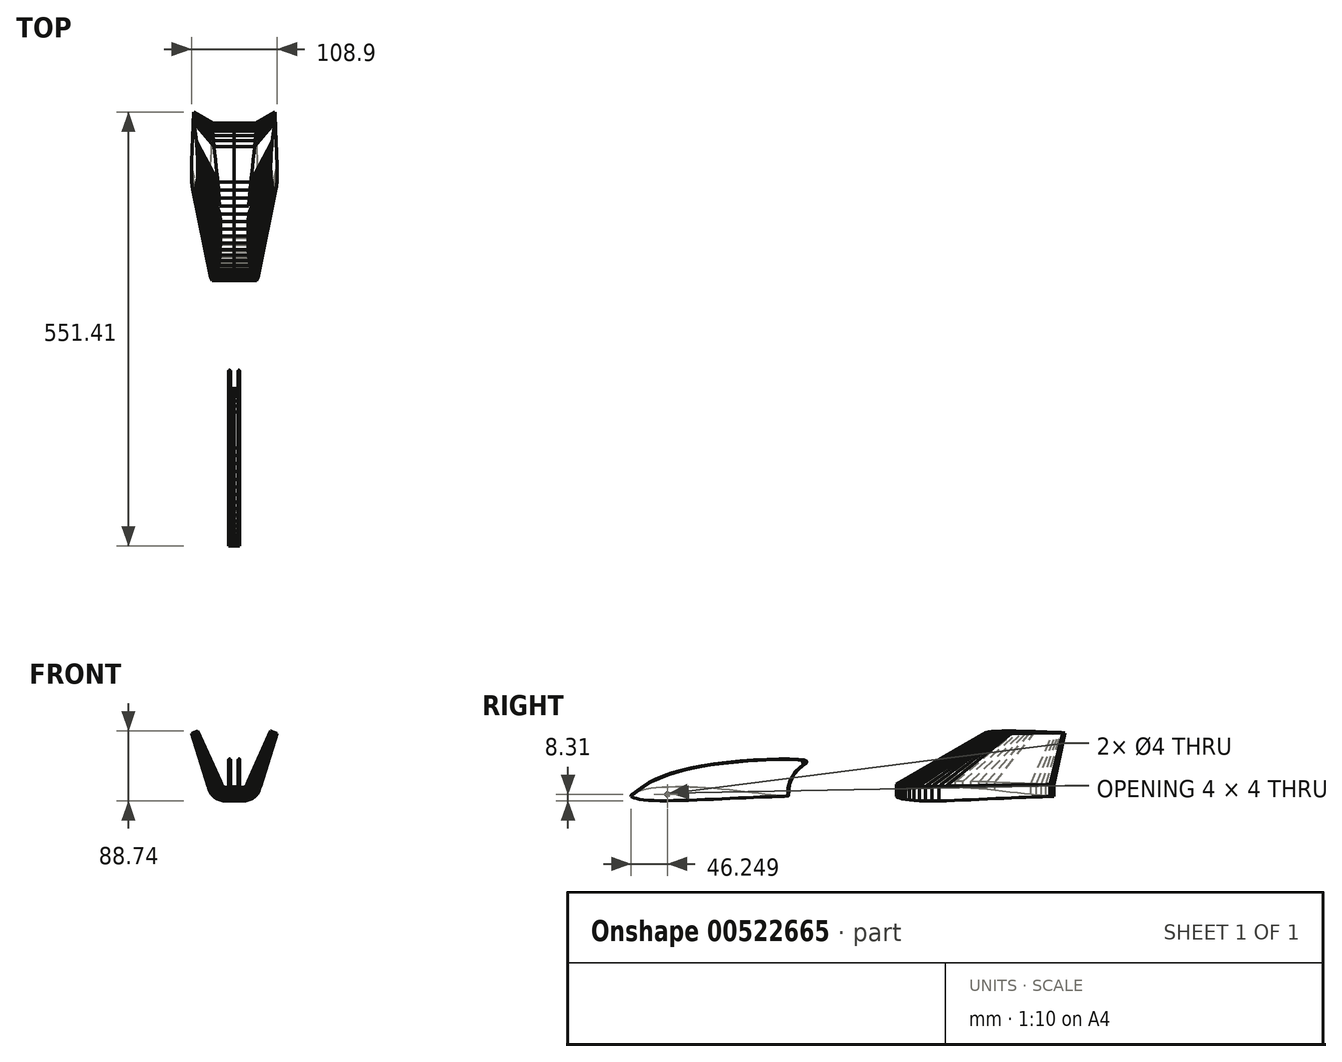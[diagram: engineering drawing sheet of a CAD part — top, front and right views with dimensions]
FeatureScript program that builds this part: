
annotation { "Feature Type Name" : "Feature", "Feature Type Description" : "" }
export const myFeature = defineFeature(function(context is Context, id is Id, definition is map)
    precondition{}
    {
        {
            var Q0;
            Q0=qCreatedBy(makeId("Right.planeOp"),FACE);
            var sketch = newSketch(context, id + "F0", { "sketchPlane" : qUnion([Q0])});
            skLineSegment(sketch, "E0.MirrorCS", {"start": v(124.06, -2.37) * mm, "end": v(124.69, -2.32) * mm});
            skLineSegment(sketch, "E1.MirrorCS", {"start": v(119.29, -2.62) * mm, "end": v(122.24, -2.48) * mm});
            skLineSegment(sketch, "E2.MirrorCS", {"start": v(122.24, -2.48) * mm, "end": v(124.06, -2.37) * mm});
            skLineSegment(sketch, "E3.MirrorCS", {"start": v(124.69, -2.32) * mm, "end": v(124.05, -2.33) * mm});
            skLineSegment(sketch, "E4.MirrorCS", {"start": v(124.05, -2.33) * mm, "end": v(122.1, -2.3) * mm});
            skLineSegment(sketch, "E5.MirrorCS", {"start": v(122.1, -2.3) * mm, "end": v(118.9, -2.2) * mm});
            skLineSegment(sketch, "E6.MirrorCS", {"start": v(-75.31, -2.32) * mm, "end": v(-75.15, -2.84) * mm});
            skLineSegment(sketch, "E7.MirrorCS", {"start": v(-61.33, 5) * mm, "end": v(-65.79, 3.73) * mm});
            skLineSegment(sketch, "E8.MirrorCS", {"start": v(115.22, -2.78) * mm, "end": v(119.29, -2.62) * mm});
            skLineSegment(sketch, "E9.MirrorCS", {"start": v(-65.79, 3.73) * mm, "end": v(-69.42, 2.35) * mm});
            skLineSegment(sketch, "E10.MirrorCS", {"start": v(-69.42, 2.35) * mm, "end": v(-72.2, 0.9) * mm});
            skLineSegment(sketch, "E11.MirrorCS", {"start": v(-72.2, 0.9) * mm, "end": v(-74.13, -0.52) * mm});
            skLineSegment(sketch, "E12.MirrorCS", {"start": v(-74.13, -0.52) * mm, "end": v(-75.2, -1.8) * mm});
            skLineSegment(sketch, "E13.MirrorCS", {"start": v(-75.2, -1.8) * mm, "end": v(-75.31, -2.32) * mm});
            skLineSegment(sketch, "E14.MirrorCS", {"start": v(-75.15, -2.84) * mm, "end": v(-73.93, -3.77) * mm});
            skLineSegment(sketch, "E15.MirrorCS", {"start": v(-73.93, -3.77) * mm, "end": v(-71.65, -4.72) * mm});
            skLineSegment(sketch, "E16.MirrorCS", {"start": v(118.9, -2.2) * mm, "end": v(114.52, -1.97) * mm});
            skLineSegment(sketch, "E17.MirrorCS", {"start": v(-68.38, -5.63) * mm, "end": v(-64.18, -6.45) * mm});
            skLineSegment(sketch, "E18.MirrorCS", {"start": v(-71.65, -4.72) * mm, "end": v(-68.38, -5.63) * mm});
            skLineSegment(sketch, "E19.MirrorCS", {"start": v(114.52, -1.97) * mm, "end": v(109.03, -1.58) * mm});
            skLineSegment(sketch, "E20.MirrorCS", {"start": v(109.03, -1.58) * mm, "end": v(102.52, -1) * mm});
            skLineSegment(sketch, "E21.MirrorCS", {"start": v(103.9, -3.2) * mm, "end": v(110.07, -2.97) * mm});
            skLineSegment(sketch, "E22.MirrorCS", {"start": v(110.07, -2.97) * mm, "end": v(115.22, -2.78) * mm});
            skLineSegment(sketch, "E23.MirrorCS", {"start": v(87, 0.67) * mm, "end": v(78.26, 1.71) * mm});
            skLineSegment(sketch, "E24.MirrorCS", {"start": v(-56.06, 6.14) * mm, "end": v(-61.33, 5) * mm});
            skLineSegment(sketch, "E25.MirrorCS", {"start": v(78.26, 1.71) * mm, "end": v(69.02, 2.84) * mm});
            skLineSegment(sketch, "E26.MirrorCS", {"start": v(-30.42, -8.31) * mm, "end": v(-21.47, -8.22) * mm});
            skLineSegment(sketch, "E27.MirrorCS", {"start": v(69.02, 2.84) * mm, "end": v(59.42, 3.99) * mm});
            skLineSegment(sketch, "E28.MirrorCS", {"start": v(-21.47, -8.22) * mm, "end": v(-11.95, -8) * mm});
            skLineSegment(sketch, "E29.MirrorCS", {"start": v(59.42, 3.99) * mm, "end": v(49.56, 5.1) * mm});
            skLineSegment(sketch, "E30.MirrorCS", {"start": v(-11.95, -8) * mm, "end": v(-1.98, -7.68) * mm});
            skLineSegment(sketch, "E31.MirrorCS", {"start": v(49.56, 5.1) * mm, "end": v(39.54, 6.12) * mm});
            skLineSegment(sketch, "E32.MirrorCS", {"start": v(-1.98, -7.68) * mm, "end": v(8.35, -7.28) * mm});
            skLineSegment(sketch, "E33.MirrorCS", {"start": v(8.35, -7.28) * mm, "end": v(18.91, -6.83) * mm});
            skLineSegment(sketch, "E34.MirrorCS", {"start": v(39.54, 6.12) * mm, "end": v(29.44, 7.02) * mm});
            skLineSegment(sketch, "E35.MirrorCS", {"start": v(18.91, -6.83) * mm, "end": v(29.6, -6.36) * mm});
            skLineSegment(sketch, "E36.MirrorCS", {"start": v(29.44, 7.02) * mm, "end": v(19.35, 7.76) * mm});
            skLineSegment(sketch, "E37.MirrorCS", {"start": v(29.6, -6.36) * mm, "end": v(40.26, -5.87) * mm});
            skLineSegment(sketch, "E38.MirrorCS", {"start": v(19.35, 7.76) * mm, "end": v(9.36, 8.35) * mm});
            skLineSegment(sketch, "E39.MirrorCS", {"start": v(40.26, -5.87) * mm, "end": v(50.78, -5.4) * mm});
            skLineSegment(sketch, "E40.MirrorCS", {"start": v(9.36, 8.35) * mm, "end": v(-0.44, 8.76) * mm});
            skLineSegment(sketch, "E41.MirrorCS", {"start": v(50.78, -5.4) * mm, "end": v(61.02, -4.95) * mm});
            skLineSegment(sketch, "E42.MirrorCS", {"start": v(-0.44, 8.76) * mm, "end": v(-9.94, 8.99) * mm});
            skLineSegment(sketch, "E43.MirrorCS", {"start": v(-19.05, 9.02) * mm, "end": v(-27.68, 8.86) * mm});
            skLineSegment(sketch, "E44.MirrorCS", {"start": v(70.86, -4.52) * mm, "end": v(80.18, -4.13) * mm});
            skLineSegment(sketch, "E45.MirrorCS", {"start": v(61.02, -4.95) * mm, "end": v(70.86, -4.52) * mm});
            skLineSegment(sketch, "E46.MirrorCS", {"start": v(-9.94, 8.99) * mm, "end": v(-19.05, 9.02) * mm});
            skLineSegment(sketch, "E47.MirrorCS", {"start": v(-27.68, 8.86) * mm, "end": v(-35.76, 8.48) * mm});
            skLineSegment(sketch, "E48.MirrorCS", {"start": v(80.18, -4.13) * mm, "end": v(88.87, -3.77) * mm});
            skLineSegment(sketch, "E49.MirrorCS", {"start": v(-64.18, -6.45) * mm, "end": v(-59.07, -7.15) * mm});
            skLineSegment(sketch, "E50.MirrorCS", {"start": v(-35.76, 8.48) * mm, "end": v(-43.22, 7.9) * mm});
            skLineSegment(sketch, "E51.MirrorCS", {"start": v(88.87, -3.77) * mm, "end": v(96.8, -3.46) * mm});
            skLineSegment(sketch, "E52.MirrorCS", {"start": v(-59.07, -7.15) * mm, "end": v(-53.1, -7.7) * mm});
            skLineSegment(sketch, "E53.MirrorCS", {"start": v(102.52, -1) * mm, "end": v(95.14, -0.25) * mm});
            skLineSegment(sketch, "E54.MirrorCS", {"start": v(-43.22, 7.9) * mm, "end": v(-50, 7.11) * mm});
            skLineSegment(sketch, "E55.MirrorCS", {"start": v(-53.1, -7.7) * mm, "end": v(-46.3, -8.07) * mm});
            skLineSegment(sketch, "E56.MirrorCS", {"start": v(96.8, -3.46) * mm, "end": v(103.9, -3.2) * mm});
            skLineSegment(sketch, "E57.MirrorCS", {"start": v(-50, 7.11) * mm, "end": v(-56.06, 6.14) * mm});
            skLineSegment(sketch, "E58.MirrorCS", {"start": v(95.14, -0.25) * mm, "end": v(87, 0.67) * mm});
            skLineSegment(sketch, "E59.MirrorCS", {"start": v(-46.3, -8.07) * mm, "end": v(-38.72, -8.27) * mm});
            skLineSegment(sketch, "E60.MirrorCS", {"start": v(-38.72, -8.27) * mm, "end": v(-30.42, -8.31) * mm});
            skLineSegment(sketch, "E61.MirrorCS", {"start": v(-213.27, -2.07) * mm, "end": v(-212.64, -2.02) * mm});
            skLineSegment(sketch, "E62.MirrorCS", {"start": v(-218.04, -2.32) * mm, "end": v(-215.09, -2.18) * mm});
            skLineSegment(sketch, "E63.MirrorCS", {"start": v(-215.09, -2.18) * mm, "end": v(-213.27, -2.07) * mm});
            skLineSegment(sketch, "E64.MirrorCS", {"start": v(-212.64, -2.02) * mm, "end": v(-213.29, -2.03) * mm});
            skLineSegment(sketch, "E65.MirrorCS", {"start": v(-213.29, -2.03) * mm, "end": v(-215.22, -2) * mm});
            skLineSegment(sketch, "E66.MirrorCS", {"start": v(-215.22, -2) * mm, "end": v(-218.42, -1.9) * mm});
            skLineSegment(sketch, "E67.MirrorCS", {"start": v(-412.64, -2.02) * mm, "end": v(-412.49, -2.54) * mm});
            skLineSegment(sketch, "E68.MirrorCS", {"start": v(-398.66, 5.3) * mm, "end": v(-403.12, 4.03) * mm});
            skLineSegment(sketch, "E69.MirrorCS", {"start": v(-222.12, -2.48) * mm, "end": v(-218.04, -2.32) * mm});
            skLineSegment(sketch, "E70.MirrorCS", {"start": v(-403.12, 4.03) * mm, "end": v(-406.75, 2.65) * mm});
            skLineSegment(sketch, "E71.MirrorCS", {"start": v(-406.75, 2.65) * mm, "end": v(-409.53, 1.2) * mm});
            skLineSegment(sketch, "E72.MirrorCS", {"start": v(-409.53, 1.2) * mm, "end": v(-411.46, -0.22) * mm});
            skLineSegment(sketch, "E73.MirrorCS", {"start": v(-411.46, -0.22) * mm, "end": v(-412.52, -1.5) * mm});
            skLineSegment(sketch, "E74.MirrorCS", {"start": v(-412.52, -1.5) * mm, "end": v(-412.64, -2.02) * mm});
            skLineSegment(sketch, "E75.MirrorCS", {"start": v(-412.49, -2.54) * mm, "end": v(-411.26, -3.47) * mm});
            skLineSegment(sketch, "E76.MirrorCS", {"start": v(-411.26, -3.47) * mm, "end": v(-408.98, -4.42) * mm});
            skLineSegment(sketch, "E77.MirrorCS", {"start": v(-218.42, -1.9) * mm, "end": v(-222.8, -1.67) * mm});
            skLineSegment(sketch, "E78.MirrorCS", {"start": v(-405.72, -5.33) * mm, "end": v(-401.5, -6.15) * mm});
            skLineSegment(sketch, "E79.MirrorCS", {"start": v(-408.98, -4.42) * mm, "end": v(-405.72, -5.33) * mm});
            skLineSegment(sketch, "E80.MirrorCS", {"start": v(-222.8, -1.67) * mm, "end": v(-228.3, -1.28) * mm});
            skLineSegment(sketch, "E81.MirrorCS", {"start": v(-228.3, -1.28) * mm, "end": v(-234.81, -0.7) * mm});
            skLineSegment(sketch, "E82.MirrorCS", {"start": v(-233.43, -2.9) * mm, "end": v(-227.27, -2.67) * mm});
            skLineSegment(sketch, "E83.MirrorCS", {"start": v(-227.27, -2.67) * mm, "end": v(-222.12, -2.48) * mm});
            skLineSegment(sketch, "E84.MirrorCS", {"start": v(-250.32, 0.97) * mm, "end": v(-259.07, 2.01) * mm});
            skLineSegment(sketch, "E85.MirrorCS", {"start": v(-393.39, 6.44) * mm, "end": v(-398.66, 5.3) * mm});
            skLineSegment(sketch, "E86.MirrorCS", {"start": v(-259.07, 2.01) * mm, "end": v(-268.3, 3.14) * mm});
            skLineSegment(sketch, "E87.MirrorCS", {"start": v(-367.75, -8.01) * mm, "end": v(-358.8, -7.92) * mm});
            skLineSegment(sketch, "E88.MirrorCS", {"start": v(-268.3, 3.14) * mm, "end": v(-277.91, 4.29) * mm});
            skLineSegment(sketch, "E89.MirrorCS", {"start": v(-358.8, -7.92) * mm, "end": v(-349.29, -7.7) * mm});
            skLineSegment(sketch, "E90.MirrorCS", {"start": v(-277.91, 4.29) * mm, "end": v(-287.77, 5.4) * mm});
            skLineSegment(sketch, "E91.MirrorCS", {"start": v(-349.29, -7.7) * mm, "end": v(-339.31, -7.38) * mm});
            skLineSegment(sketch, "E92.MirrorCS", {"start": v(-287.77, 5.4) * mm, "end": v(-297.79, 6.42) * mm});
            skLineSegment(sketch, "E93.MirrorCS", {"start": v(-339.31, -7.38) * mm, "end": v(-328.98, -6.98) * mm});
            skLineSegment(sketch, "E94.MirrorCS", {"start": v(-328.98, -6.98) * mm, "end": v(-318.42, -6.53) * mm});
            skLineSegment(sketch, "E95.MirrorCS", {"start": v(-297.79, 6.42) * mm, "end": v(-307.89, 7.32) * mm});
            skLineSegment(sketch, "E96.MirrorCS", {"start": v(-318.42, -6.53) * mm, "end": v(-307.74, -6.06) * mm});
            skLineSegment(sketch, "E97.MirrorCS", {"start": v(-307.89, 7.32) * mm, "end": v(-317.98, 8.06) * mm});
            skLineSegment(sketch, "E98.MirrorCS", {"start": v(-307.74, -6.06) * mm, "end": v(-297.07, -5.57) * mm});
            skLineSegment(sketch, "E99.MirrorCS", {"start": v(-317.98, 8.06) * mm, "end": v(-327.97, 8.65) * mm});
            skLineSegment(sketch, "E100.MirrorCS", {"start": v(-297.07, -5.57) * mm, "end": v(-286.55, -5.1) * mm});
            skLineSegment(sketch, "E101.MirrorCS", {"start": v(-327.97, 8.65) * mm, "end": v(-337.77, 9.06) * mm});
            skLineSegment(sketch, "E102.MirrorCS", {"start": v(-286.55, -5.1) * mm, "end": v(-276.3, -4.65) * mm});
            skLineSegment(sketch, "E103.MirrorCS", {"start": v(-337.77, 9.06) * mm, "end": v(-347.27, 9.29) * mm});
            skLineSegment(sketch, "E104.MirrorCS", {"start": v(-356.38, 9.32) * mm, "end": v(-365.01, 9.16) * mm});
            skLineSegment(sketch, "E105.MirrorCS", {"start": v(-266.47, -4.22) * mm, "end": v(-257.15, -3.83) * mm});
            skLineSegment(sketch, "E106.MirrorCS", {"start": v(-276.3, -4.65) * mm, "end": v(-266.47, -4.22) * mm});
            skLineSegment(sketch, "E107.MirrorCS", {"start": v(-347.27, 9.29) * mm, "end": v(-356.38, 9.32) * mm});
            skLineSegment(sketch, "E108.MirrorCS", {"start": v(-365.01, 9.16) * mm, "end": v(-373.1, 8.78) * mm});
            skLineSegment(sketch, "E109.MirrorCS", {"start": v(-257.15, -3.83) * mm, "end": v(-248.46, -3.47) * mm});
            skLineSegment(sketch, "E110.MirrorCS", {"start": v(-401.5, -6.15) * mm, "end": v(-396.4, -6.85) * mm});
            skLineSegment(sketch, "E111.MirrorCS", {"start": v(-373.1, 8.78) * mm, "end": v(-380.56, 8.2) * mm});
            skLineSegment(sketch, "E112.MirrorCS", {"start": v(-248.46, -3.47) * mm, "end": v(-240.52, -3.16) * mm});
            skLineSegment(sketch, "E113.MirrorCS", {"start": v(-396.4, -6.85) * mm, "end": v(-390.43, -7.4) * mm});
            skLineSegment(sketch, "E114.MirrorCS", {"start": v(-234.81, -0.7) * mm, "end": v(-242.2, 0.05) * mm});
            skLineSegment(sketch, "E115.MirrorCS", {"start": v(-380.56, 8.2) * mm, "end": v(-387.34, 7.41) * mm});
            skLineSegment(sketch, "E116.MirrorCS", {"start": v(-390.43, -7.4) * mm, "end": v(-383.63, -7.77) * mm});
            skLineSegment(sketch, "E117.MirrorCS", {"start": v(-240.52, -3.16) * mm, "end": v(-233.43, -2.9) * mm});
            skLineSegment(sketch, "E118.MirrorCS", {"start": v(-387.34, 7.41) * mm, "end": v(-393.39, 6.44) * mm});
            skLineSegment(sketch, "E119.MirrorCS", {"start": v(-242.2, 0.05) * mm, "end": v(-250.32, 0.97) * mm});
            skLineSegment(sketch, "E120.MirrorCS", {"start": v(-383.63, -7.77) * mm, "end": v(-376.06, -7.97) * mm});
            skLineSegment(sketch, "E121.MirrorCS", {"start": v(-376.06, -7.97) * mm, "end": v(-367.75, -8.01) * mm});
            skSolve(sketch);
        }
        {
            var Q0;
            Q0=qCreatedBy(makeId("Front.planeOp"),FACE);
            var sketch = newSketch(context, id + "F1", { "sketchPlane" : qUnion([Q0])});
            skLineSegment(sketch, "E122", {"start": v(0, 0) * mm, "end": v(-10, 0) * mm});
            skFitSpline(sketch, "E123", {"points": [v(-10, 0) * mm, v(-25.62, 13.4) * mm], "startDerivative": vector(-39.4, 0) * mm, "endDerivative": vector(-4.61, 11.92) * mm});
            skSolve(sketch);
        }
        {
            var Q0;
            Q0=makeQuery(id+"F0.imprint","IMPRINT",FACE,{"disambiguationData":[TD([[makeQuery(id+"F0.imprint","IMPRINT",EDGE,{"derivedFrom":sQuery(id+"F0.wireOp",EDGE,"E0.MirrorCS")}),1.0]])]});
            var Q1;
            Q1=sQuery(id+"F1.wireOp",EDGE,"E122");
            var Q2;
            Q2=sQuery(id+"F1.wireOp",EDGE,"E123");
            sweep(context, id + "F2", {"profiles" : qUnion([Q0]), "path" : qUnion([Q1, Q2])});
        }
        {
            var Q0;
            Q0=makeQuery(id+"F2.opSweep","CAP_FACE",FACE,{"disambiguationData":[OSD([sQuery(id+"F0.wireOp",EDGE,"E0.MirrorCS"),sQuery(id+"F0.wireOp",EDGE,"E1.MirrorCS"),sQuery(id+"F0.wireOp",EDGE,"E2.MirrorCS"),sQuery(id+"F0.wireOp",EDGE,"E3.MirrorCS"),sQuery(id+"F0.wireOp",EDGE,"E4.MirrorCS"),sQuery(id+"F0.wireOp",EDGE,"E5.MirrorCS"),sQuery(id+"F0.wireOp",EDGE,"E6.MirrorCS"),sQuery(id+"F0.wireOp",EDGE,"E7.MirrorCS"),sQuery(id+"F0.wireOp",EDGE,"E8.MirrorCS"),sQuery(id+"F0.wireOp",EDGE,"E9.MirrorCS"),sQuery(id+"F0.wireOp",EDGE,"E10.MirrorCS"),sQuery(id+"F0.wireOp",EDGE,"E11.MirrorCS"),sQuery(id+"F0.wireOp",EDGE,"E12.MirrorCS"),sQuery(id+"F0.wireOp",EDGE,"E13.MirrorCS"),sQuery(id+"F0.wireOp",EDGE,"E14.MirrorCS"),sQuery(id+"F0.wireOp",EDGE,"E15.MirrorCS"),sQuery(id+"F0.wireOp",EDGE,"E16.MirrorCS"),sQuery(id+"F0.wireOp",EDGE,"E17.MirrorCS"),sQuery(id+"F0.wireOp",EDGE,"E18.MirrorCS"),sQuery(id+"F0.wireOp",EDGE,"E19.MirrorCS"),sQuery(id+"F0.wireOp",EDGE,"E20.MirrorCS"),sQuery(id+"F0.wireOp",EDGE,"E21.MirrorCS"),sQuery(id+"F0.wireOp",EDGE,"E22.MirrorCS"),sQuery(id+"F0.wireOp",EDGE,"E23.MirrorCS"),sQuery(id+"F0.wireOp",EDGE,"E24.MirrorCS"),sQuery(id+"F0.wireOp",EDGE,"E25.MirrorCS"),sQuery(id+"F0.wireOp",EDGE,"E26.MirrorCS"),sQuery(id+"F0.wireOp",EDGE,"E27.MirrorCS"),sQuery(id+"F0.wireOp",EDGE,"E28.MirrorCS"),sQuery(id+"F0.wireOp",EDGE,"E29.MirrorCS"),sQuery(id+"F0.wireOp",EDGE,"E30.MirrorCS"),sQuery(id+"F0.wireOp",EDGE,"E31.MirrorCS"),sQuery(id+"F0.wireOp",EDGE,"E32.MirrorCS"),sQuery(id+"F0.wireOp",EDGE,"E33.MirrorCS"),sQuery(id+"F0.wireOp",EDGE,"E34.MirrorCS"),sQuery(id+"F0.wireOp",EDGE,"E35.MirrorCS"),sQuery(id+"F0.wireOp",EDGE,"E36.MirrorCS"),sQuery(id+"F0.wireOp",EDGE,"E37.MirrorCS"),sQuery(id+"F0.wireOp",EDGE,"E38.MirrorCS"),sQuery(id+"F0.wireOp",EDGE,"E39.MirrorCS"),sQuery(id+"F0.wireOp",EDGE,"E40.MirrorCS"),sQuery(id+"F0.wireOp",EDGE,"E41.MirrorCS"),sQuery(id+"F0.wireOp",EDGE,"E42.MirrorCS"),sQuery(id+"F0.wireOp",EDGE,"E43.MirrorCS"),sQuery(id+"F0.wireOp",EDGE,"E44.MirrorCS"),sQuery(id+"F0.wireOp",EDGE,"E45.MirrorCS"),sQuery(id+"F0.wireOp",EDGE,"E46.MirrorCS"),sQuery(id+"F0.wireOp",EDGE,"E47.MirrorCS"),sQuery(id+"F0.wireOp",EDGE,"E48.MirrorCS"),sQuery(id+"F0.wireOp",EDGE,"E49.MirrorCS"),sQuery(id+"F0.wireOp",EDGE,"E50.MirrorCS"),sQuery(id+"F0.wireOp",EDGE,"E51.MirrorCS"),sQuery(id+"F0.wireOp",EDGE,"E52.MirrorCS"),sQuery(id+"F0.wireOp",EDGE,"E53.MirrorCS"),sQuery(id+"F0.wireOp",EDGE,"E54.MirrorCS"),sQuery(id+"F0.wireOp",EDGE,"E55.MirrorCS"),sQuery(id+"F0.wireOp",EDGE,"E56.MirrorCS"),sQuery(id+"F0.wireOp",EDGE,"E57.MirrorCS"),sQuery(id+"F0.wireOp",EDGE,"E58.MirrorCS"),sQuery(id+"F0.wireOp",EDGE,"E59.MirrorCS"),sQuery(id+"F0.wireOp",EDGE,"E60.MirrorCS"),sQuery(id+"F1.wireOp",VERTEX,"E123.end")])],"isStart":false});
            cPlane(context, id + "F3", {"entities" : qUnion([Q0]), "cplaneType" : CPlaneType.OFFSET, "offset" : 70 * mm, "width" : 150 * mm, "height" : 150 * mm});
        }
        {
            var Q0;
            Q0=qCreatedBy(id+"F3.planeOp",FACE);
            var sketch = newSketch(context, id + "F4", { "sketchPlane" : qUnion([Q0])});
            skLineSegment(sketch, "E124.MirrorCS", {"start": v(-19.92, 138.46) * mm, "end": v(-19.9, 138.77) * mm});
            skLineSegment(sketch, "E125.MirrorCS", {"start": v(-19.9, 138.45) * mm, "end": v(-19.9, 137.48) * mm});
            skLineSegment(sketch, "E126.MirrorCS", {"start": v(-19.9, 138.77) * mm, "end": v(-19.9, 138.45) * mm});
            skLineSegment(sketch, "E127.MirrorCS", {"start": v(-19.65, 38.83) * mm, "end": v(-19.9, 38.77) * mm});
            skLineSegment(sketch, "E128.MirrorCS", {"start": v(-19.98, 137.55) * mm, "end": v(-19.92, 138.46) * mm});
            skLineSegment(sketch, "E129.MirrorCS", {"start": v(-20.16, 38.85) * mm, "end": v(-20.63, 39.46) * mm});
            skLineSegment(sketch, "E130.MirrorCS", {"start": v(-20.05, 136.07) * mm, "end": v(-19.98, 137.55) * mm});
            skLineSegment(sketch, "E131.MirrorCS", {"start": v(-19.9, 38.77) * mm, "end": v(-20.16, 38.85) * mm});
            skLineSegment(sketch, "E132.MirrorCS", {"start": v(-19, 39.36) * mm, "end": v(-19.65, 38.83) * mm});
            skLineSegment(sketch, "E133.MirrorCS", {"start": v(-20.23, 131.46) * mm, "end": v(-20.13, 134.04) * mm});
            skLineSegment(sketch, "E134.MirrorCS", {"start": v(-21.56, 42.24) * mm, "end": v(-21.97, 44.34) * mm});
            skLineSegment(sketch, "E135.MirrorCS", {"start": v(-17.57, 41.72) * mm, "end": v(-18.29, 40.33) * mm});
            skLineSegment(sketch, "E136.MirrorCS", {"start": v(-20.63, 39.46) * mm, "end": v(-21.1, 40.6) * mm});
            skLineSegment(sketch, "E137.MirrorCS", {"start": v(-19.72, 133.7) * mm, "end": v(-19.53, 130.94) * mm});
            skLineSegment(sketch, "E138.MirrorCS", {"start": v(-19.9, 137.48) * mm, "end": v(-19.84, 135.88) * mm});
            skLineSegment(sketch, "E139.MirrorCS", {"start": v(-20.34, 128.38) * mm, "end": v(-20.23, 131.46) * mm});
            skLineSegment(sketch, "E140.MirrorCS", {"start": v(-18.29, 40.33) * mm, "end": v(-19, 39.36) * mm});
            skLineSegment(sketch, "E141.MirrorCS", {"start": v(-20.13, 134.04) * mm, "end": v(-20.05, 136.07) * mm});
            skLineSegment(sketch, "E142.MirrorCS", {"start": v(-19.84, 135.88) * mm, "end": v(-19.72, 133.7) * mm});
            skLineSegment(sketch, "E143.MirrorCS", {"start": v(-16.87, 43.54) * mm, "end": v(-17.57, 41.72) * mm});
            skLineSegment(sketch, "E144.MirrorCS", {"start": v(-21.1, 40.6) * mm, "end": v(-21.56, 42.24) * mm});
            skLineSegment(sketch, "E145.MirrorCS", {"start": v(-16.24, 45.76) * mm, "end": v(-16.87, 43.54) * mm});
            skLineSegment(sketch, "E146.MirrorCS", {"start": v(-22.32, 46.9) * mm, "end": v(-22.59, 49.88) * mm});
            skLineSegment(sketch, "E147.MirrorCS", {"start": v(-14.25, 71.46) * mm, "end": v(-14.23, 66.9) * mm});
            skLineSegment(sketch, "E148.MirrorCS", {"start": v(-20.63, 120.86) * mm, "end": v(-20.47, 124.83) * mm});
            skLineSegment(sketch, "E149.MirrorCS", {"start": v(-22.16, 85.89) * mm, "end": v(-21.92, 91.23) * mm});
            skLineSegment(sketch, "E150.MirrorCS", {"start": v(-22.74, 70.45) * mm, "end": v(-22.58, 75.44) * mm});
            skLineSegment(sketch, "E151.MirrorCS", {"start": v(-21.68, 96.56) * mm, "end": v(-21.44, 101.82) * mm});
            skLineSegment(sketch, "E152.MirrorCS", {"start": v(-18.4, 119.93) * mm, "end": v(-17.88, 115.56) * mm});
            skLineSegment(sketch, "E153.MirrorCS", {"start": v(-15.67, 48.4) * mm, "end": v(-16.24, 45.76) * mm});
            skLineSegment(sketch, "E154.MirrorCS", {"start": v(-14.86, 86.1) * mm, "end": v(-14.57, 81.1) * mm});
            skLineSegment(sketch, "E155.MirrorCS", {"start": v(-22.58, 75.44) * mm, "end": v(-22.38, 80.6) * mm});
            skLineSegment(sketch, "E156.MirrorCS", {"start": v(-14.8, 54.82) * mm, "end": v(-15.19, 51.43) * mm});
            skLineSegment(sketch, "E157.MirrorCS", {"start": v(-14.36, 76.21) * mm, "end": v(-14.25, 71.46) * mm});
            skLineSegment(sketch, "E158.MirrorCS", {"start": v(-22.38, 80.6) * mm, "end": v(-22.16, 85.89) * mm});
            skLineSegment(sketch, "E159.MirrorCS", {"start": v(-17.32, 110.94) * mm, "end": v(-16.75, 106.14) * mm});
            skLineSegment(sketch, "E160.MirrorCS", {"start": v(-21.44, 101.82) * mm, "end": v(-21.21, 106.94) * mm});
            skLineSegment(sketch, "E161.MirrorCS", {"start": v(-19.53, 130.94) * mm, "end": v(-19.24, 127.69) * mm});
            skLineSegment(sketch, "E162.MirrorCS", {"start": v(-21.97, 44.34) * mm, "end": v(-22.32, 46.9) * mm});
            skLineSegment(sketch, "E163.MirrorCS", {"start": v(-22.88, 57.07) * mm, "end": v(-22.9, 61.22) * mm});
            skLineSegment(sketch, "E164.MirrorCS", {"start": v(-20.47, 124.83) * mm, "end": v(-20.34, 128.38) * mm});
            skLineSegment(sketch, "E165.MirrorCS", {"start": v(-14.5, 58.55) * mm, "end": v(-14.8, 54.82) * mm});
            skLineSegment(sketch, "E166.MirrorCS", {"start": v(-15.68, 96.2) * mm, "end": v(-15.23, 91.15) * mm});
            skLineSegment(sketch, "E167.MirrorCS", {"start": v(-22.9, 61.22) * mm, "end": v(-22.85, 65.7) * mm});
            skLineSegment(sketch, "E168.MirrorCS", {"start": v(-21.92, 91.23) * mm, "end": v(-21.68, 96.56) * mm});
            skLineSegment(sketch, "E169.MirrorCS", {"start": v(-17.88, 115.56) * mm, "end": v(-17.32, 110.94) * mm});
            skLineSegment(sketch, "E170.MirrorCS", {"start": v(-19.24, 127.69) * mm, "end": v(-18.86, 124) * mm});
            skLineSegment(sketch, "E171.MirrorCS", {"start": v(-22.59, 49.88) * mm, "end": v(-22.78, 53.28) * mm});
            skLineSegment(sketch, "E172.MirrorCS", {"start": v(-14.57, 81.1) * mm, "end": v(-14.36, 76.21) * mm});
            skLineSegment(sketch, "E173.MirrorCS", {"start": v(-16.75, 106.14) * mm, "end": v(-16.2, 101.21) * mm});
            skLineSegment(sketch, "E174.MirrorCS", {"start": v(-22.78, 53.28) * mm, "end": v(-22.88, 57.07) * mm});
            skLineSegment(sketch, "E175.MirrorCS", {"start": v(-18.86, 124) * mm, "end": v(-18.4, 119.93) * mm});
            skLineSegment(sketch, "E176.MirrorCS", {"start": v(-16.2, 101.21) * mm, "end": v(-15.68, 96.2) * mm});
            skLineSegment(sketch, "E177.MirrorCS", {"start": v(-14.23, 66.9) * mm, "end": v(-14.31, 62.59) * mm});
            skLineSegment(sketch, "E178.MirrorCS", {"start": v(-21, 111.86) * mm, "end": v(-20.8, 116.52) * mm});
            skLineSegment(sketch, "E179.MirrorCS", {"start": v(-15.19, 51.43) * mm, "end": v(-15.67, 48.4) * mm});
            skLineSegment(sketch, "E180.MirrorCS", {"start": v(-14.31, 62.59) * mm, "end": v(-14.5, 58.55) * mm});
            skLineSegment(sketch, "E181.MirrorCS", {"start": v(-22.85, 65.7) * mm, "end": v(-22.74, 70.45) * mm});
            skLineSegment(sketch, "E182.MirrorCS", {"start": v(-15.23, 91.15) * mm, "end": v(-14.86, 86.1) * mm});
            skLineSegment(sketch, "E183.MirrorCS", {"start": v(-20.8, 116.52) * mm, "end": v(-20.63, 120.86) * mm});
            skLineSegment(sketch, "E184.MirrorCS", {"start": v(-21.21, 106.94) * mm, "end": v(-21, 111.86) * mm});
            skSolve(sketch);
        }
        {
            var Q1;
            Q1=makeQuery(id+"F2.opSweep","CAP_FACE",FACE,{"disambiguationData":[OSD([sQuery(id+"F0.wireOp",EDGE,"E0.MirrorCS"),sQuery(id+"F0.wireOp",EDGE,"E1.MirrorCS"),sQuery(id+"F0.wireOp",EDGE,"E2.MirrorCS"),sQuery(id+"F0.wireOp",EDGE,"E3.MirrorCS"),sQuery(id+"F0.wireOp",EDGE,"E4.MirrorCS"),sQuery(id+"F0.wireOp",EDGE,"E5.MirrorCS"),sQuery(id+"F0.wireOp",EDGE,"E6.MirrorCS"),sQuery(id+"F0.wireOp",EDGE,"E7.MirrorCS"),sQuery(id+"F0.wireOp",EDGE,"E8.MirrorCS"),sQuery(id+"F0.wireOp",EDGE,"E9.MirrorCS"),sQuery(id+"F0.wireOp",EDGE,"E10.MirrorCS"),sQuery(id+"F0.wireOp",EDGE,"E11.MirrorCS"),sQuery(id+"F0.wireOp",EDGE,"E12.MirrorCS"),sQuery(id+"F0.wireOp",EDGE,"E13.MirrorCS"),sQuery(id+"F0.wireOp",EDGE,"E14.MirrorCS"),sQuery(id+"F0.wireOp",EDGE,"E15.MirrorCS"),sQuery(id+"F0.wireOp",EDGE,"E16.MirrorCS"),sQuery(id+"F0.wireOp",EDGE,"E17.MirrorCS"),sQuery(id+"F0.wireOp",EDGE,"E18.MirrorCS"),sQuery(id+"F0.wireOp",EDGE,"E19.MirrorCS"),sQuery(id+"F0.wireOp",EDGE,"E20.MirrorCS"),sQuery(id+"F0.wireOp",EDGE,"E21.MirrorCS"),sQuery(id+"F0.wireOp",EDGE,"E22.MirrorCS"),sQuery(id+"F0.wireOp",EDGE,"E23.MirrorCS"),sQuery(id+"F0.wireOp",EDGE,"E24.MirrorCS"),sQuery(id+"F0.wireOp",EDGE,"E25.MirrorCS"),sQuery(id+"F0.wireOp",EDGE,"E26.MirrorCS"),sQuery(id+"F0.wireOp",EDGE,"E27.MirrorCS"),sQuery(id+"F0.wireOp",EDGE,"E28.MirrorCS"),sQuery(id+"F0.wireOp",EDGE,"E29.MirrorCS"),sQuery(id+"F0.wireOp",EDGE,"E30.MirrorCS"),sQuery(id+"F0.wireOp",EDGE,"E31.MirrorCS"),sQuery(id+"F0.wireOp",EDGE,"E32.MirrorCS"),sQuery(id+"F0.wireOp",EDGE,"E33.MirrorCS"),sQuery(id+"F0.wireOp",EDGE,"E34.MirrorCS"),sQuery(id+"F0.wireOp",EDGE,"E35.MirrorCS"),sQuery(id+"F0.wireOp",EDGE,"E36.MirrorCS"),sQuery(id+"F0.wireOp",EDGE,"E37.MirrorCS"),sQuery(id+"F0.wireOp",EDGE,"E38.MirrorCS"),sQuery(id+"F0.wireOp",EDGE,"E39.MirrorCS"),sQuery(id+"F0.wireOp",EDGE,"E40.MirrorCS"),sQuery(id+"F0.wireOp",EDGE,"E41.MirrorCS"),sQuery(id+"F0.wireOp",EDGE,"E42.MirrorCS"),sQuery(id+"F0.wireOp",EDGE,"E43.MirrorCS"),sQuery(id+"F0.wireOp",EDGE,"E44.MirrorCS"),sQuery(id+"F0.wireOp",EDGE,"E45.MirrorCS"),sQuery(id+"F0.wireOp",EDGE,"E46.MirrorCS"),sQuery(id+"F0.wireOp",EDGE,"E47.MirrorCS"),sQuery(id+"F0.wireOp",EDGE,"E48.MirrorCS"),sQuery(id+"F0.wireOp",EDGE,"E49.MirrorCS"),sQuery(id+"F0.wireOp",EDGE,"E50.MirrorCS"),sQuery(id+"F0.wireOp",EDGE,"E51.MirrorCS"),sQuery(id+"F0.wireOp",EDGE,"E52.MirrorCS"),sQuery(id+"F0.wireOp",EDGE,"E53.MirrorCS"),sQuery(id+"F0.wireOp",EDGE,"E54.MirrorCS"),sQuery(id+"F0.wireOp",EDGE,"E55.MirrorCS"),sQuery(id+"F0.wireOp",EDGE,"E56.MirrorCS"),sQuery(id+"F0.wireOp",EDGE,"E57.MirrorCS"),sQuery(id+"F0.wireOp",EDGE,"E58.MirrorCS"),sQuery(id+"F0.wireOp",EDGE,"E59.MirrorCS"),sQuery(id+"F0.wireOp",EDGE,"E60.MirrorCS"),sQuery(id+"F1.wireOp",VERTEX,"E123.end")])],"isStart":false});
            var Q2;
            Q2=makeQuery(id+"F4.imprint","IMPRINT",FACE,{"disambiguationData":[TD([[makeQuery(id+"F4.imprint","IMPRINT",EDGE,{"derivedFrom":sQuery(id+"F4.wireOp",EDGE,"E124.MirrorCS")}),-1.0]])]});
            loft(context, id + "F5", {"operationType" : NewBodyOperationType.ADD, "sheetProfilesArray" : [{ "sheetProfileEntities" : qUnion([Q1]) }, { "sheetProfileEntities" : qUnion([Q2]) }]});
        }
        {
            var Q0;
            Q0=makeQuery(id+"F2.opSweep","SWEPT_BODY",BODY,{"disambiguationData":[OSD([sQuery(id+"F0.wireOp",EDGE,"E0.MirrorCS"),sQuery(id+"F0.wireOp",EDGE,"E1.MirrorCS"),sQuery(id+"F0.wireOp",EDGE,"E2.MirrorCS"),sQuery(id+"F0.wireOp",EDGE,"E3.MirrorCS"),sQuery(id+"F0.wireOp",EDGE,"E4.MirrorCS"),sQuery(id+"F0.wireOp",EDGE,"E5.MirrorCS"),sQuery(id+"F0.wireOp",EDGE,"E6.MirrorCS"),sQuery(id+"F0.wireOp",EDGE,"E7.MirrorCS"),sQuery(id+"F0.wireOp",EDGE,"E8.MirrorCS"),sQuery(id+"F0.wireOp",EDGE,"E9.MirrorCS"),sQuery(id+"F0.wireOp",EDGE,"E10.MirrorCS"),sQuery(id+"F0.wireOp",EDGE,"E11.MirrorCS"),sQuery(id+"F0.wireOp",EDGE,"E12.MirrorCS"),sQuery(id+"F0.wireOp",EDGE,"E13.MirrorCS"),sQuery(id+"F0.wireOp",EDGE,"E14.MirrorCS"),sQuery(id+"F0.wireOp",EDGE,"E15.MirrorCS"),sQuery(id+"F0.wireOp",EDGE,"E16.MirrorCS"),sQuery(id+"F0.wireOp",EDGE,"E17.MirrorCS"),sQuery(id+"F0.wireOp",EDGE,"E18.MirrorCS"),sQuery(id+"F0.wireOp",EDGE,"E19.MirrorCS"),sQuery(id+"F0.wireOp",EDGE,"E20.MirrorCS"),sQuery(id+"F0.wireOp",EDGE,"E21.MirrorCS"),sQuery(id+"F0.wireOp",EDGE,"E22.MirrorCS"),sQuery(id+"F0.wireOp",EDGE,"E23.MirrorCS"),sQuery(id+"F0.wireOp",EDGE,"E24.MirrorCS"),sQuery(id+"F0.wireOp",EDGE,"E25.MirrorCS"),sQuery(id+"F0.wireOp",EDGE,"E26.MirrorCS"),sQuery(id+"F0.wireOp",EDGE,"E27.MirrorCS"),sQuery(id+"F0.wireOp",EDGE,"E28.MirrorCS"),sQuery(id+"F0.wireOp",EDGE,"E29.MirrorCS"),sQuery(id+"F0.wireOp",EDGE,"E30.MirrorCS"),sQuery(id+"F0.wireOp",EDGE,"E31.MirrorCS"),sQuery(id+"F0.wireOp",EDGE,"E32.MirrorCS"),sQuery(id+"F0.wireOp",EDGE,"E33.MirrorCS"),sQuery(id+"F0.wireOp",EDGE,"E34.MirrorCS"),sQuery(id+"F0.wireOp",EDGE,"E35.MirrorCS"),sQuery(id+"F0.wireOp",EDGE,"E36.MirrorCS"),sQuery(id+"F0.wireOp",EDGE,"E37.MirrorCS"),sQuery(id+"F0.wireOp",EDGE,"E38.MirrorCS"),sQuery(id+"F0.wireOp",EDGE,"E39.MirrorCS"),sQuery(id+"F0.wireOp",EDGE,"E40.MirrorCS"),sQuery(id+"F0.wireOp",EDGE,"E41.MirrorCS"),sQuery(id+"F0.wireOp",EDGE,"E42.MirrorCS"),sQuery(id+"F0.wireOp",EDGE,"E43.MirrorCS"),sQuery(id+"F0.wireOp",EDGE,"E44.MirrorCS"),sQuery(id+"F0.wireOp",EDGE,"E45.MirrorCS"),sQuery(id+"F0.wireOp",EDGE,"E46.MirrorCS"),sQuery(id+"F0.wireOp",EDGE,"E47.MirrorCS"),sQuery(id+"F0.wireOp",EDGE,"E48.MirrorCS"),sQuery(id+"F0.wireOp",EDGE,"E49.MirrorCS"),sQuery(id+"F0.wireOp",EDGE,"E50.MirrorCS"),sQuery(id+"F0.wireOp",EDGE,"E51.MirrorCS"),sQuery(id+"F0.wireOp",EDGE,"E52.MirrorCS"),sQuery(id+"F0.wireOp",EDGE,"E53.MirrorCS"),sQuery(id+"F0.wireOp",EDGE,"E54.MirrorCS"),sQuery(id+"F0.wireOp",EDGE,"E55.MirrorCS"),sQuery(id+"F0.wireOp",EDGE,"E56.MirrorCS"),sQuery(id+"F0.wireOp",EDGE,"E57.MirrorCS"),sQuery(id+"F0.wireOp",EDGE,"E58.MirrorCS"),sQuery(id+"F0.wireOp",EDGE,"E59.MirrorCS"),sQuery(id+"F0.wireOp",EDGE,"E60.MirrorCS"),sQuery(id+"F1.wireOp",EDGE,"E123")])]});
            var Q1;
            Q1=makeQuery(id+"F2.opSweep","CAP_FACE",FACE,{"disambiguationData":[OSD([sQuery(id+"F0.wireOp",EDGE,"E0.MirrorCS"),sQuery(id+"F0.wireOp",EDGE,"E1.MirrorCS"),sQuery(id+"F0.wireOp",EDGE,"E2.MirrorCS"),sQuery(id+"F0.wireOp",EDGE,"E3.MirrorCS"),sQuery(id+"F0.wireOp",EDGE,"E4.MirrorCS"),sQuery(id+"F0.wireOp",EDGE,"E5.MirrorCS"),sQuery(id+"F0.wireOp",EDGE,"E6.MirrorCS"),sQuery(id+"F0.wireOp",EDGE,"E7.MirrorCS"),sQuery(id+"F0.wireOp",EDGE,"E8.MirrorCS"),sQuery(id+"F0.wireOp",EDGE,"E9.MirrorCS"),sQuery(id+"F0.wireOp",EDGE,"E10.MirrorCS"),sQuery(id+"F0.wireOp",EDGE,"E11.MirrorCS"),sQuery(id+"F0.wireOp",EDGE,"E12.MirrorCS"),sQuery(id+"F0.wireOp",EDGE,"E13.MirrorCS"),sQuery(id+"F0.wireOp",EDGE,"E14.MirrorCS"),sQuery(id+"F0.wireOp",EDGE,"E15.MirrorCS"),sQuery(id+"F0.wireOp",EDGE,"E16.MirrorCS"),sQuery(id+"F0.wireOp",EDGE,"E17.MirrorCS"),sQuery(id+"F0.wireOp",EDGE,"E18.MirrorCS"),sQuery(id+"F0.wireOp",EDGE,"E19.MirrorCS"),sQuery(id+"F0.wireOp",EDGE,"E20.MirrorCS"),sQuery(id+"F0.wireOp",EDGE,"E21.MirrorCS"),sQuery(id+"F0.wireOp",EDGE,"E22.MirrorCS"),sQuery(id+"F0.wireOp",EDGE,"E23.MirrorCS"),sQuery(id+"F0.wireOp",EDGE,"E24.MirrorCS"),sQuery(id+"F0.wireOp",EDGE,"E25.MirrorCS"),sQuery(id+"F0.wireOp",EDGE,"E26.MirrorCS"),sQuery(id+"F0.wireOp",EDGE,"E27.MirrorCS"),sQuery(id+"F0.wireOp",EDGE,"E28.MirrorCS"),sQuery(id+"F0.wireOp",EDGE,"E29.MirrorCS"),sQuery(id+"F0.wireOp",EDGE,"E30.MirrorCS"),sQuery(id+"F0.wireOp",EDGE,"E31.MirrorCS"),sQuery(id+"F0.wireOp",EDGE,"E32.MirrorCS"),sQuery(id+"F0.wireOp",EDGE,"E33.MirrorCS"),sQuery(id+"F0.wireOp",EDGE,"E34.MirrorCS"),sQuery(id+"F0.wireOp",EDGE,"E35.MirrorCS"),sQuery(id+"F0.wireOp",EDGE,"E36.MirrorCS"),sQuery(id+"F0.wireOp",EDGE,"E37.MirrorCS"),sQuery(id+"F0.wireOp",EDGE,"E38.MirrorCS"),sQuery(id+"F0.wireOp",EDGE,"E39.MirrorCS"),sQuery(id+"F0.wireOp",EDGE,"E40.MirrorCS"),sQuery(id+"F0.wireOp",EDGE,"E41.MirrorCS"),sQuery(id+"F0.wireOp",EDGE,"E42.MirrorCS"),sQuery(id+"F0.wireOp",EDGE,"E43.MirrorCS"),sQuery(id+"F0.wireOp",EDGE,"E44.MirrorCS"),sQuery(id+"F0.wireOp",EDGE,"E45.MirrorCS"),sQuery(id+"F0.wireOp",EDGE,"E46.MirrorCS"),sQuery(id+"F0.wireOp",EDGE,"E47.MirrorCS"),sQuery(id+"F0.wireOp",EDGE,"E48.MirrorCS"),sQuery(id+"F0.wireOp",EDGE,"E49.MirrorCS"),sQuery(id+"F0.wireOp",EDGE,"E50.MirrorCS"),sQuery(id+"F0.wireOp",EDGE,"E51.MirrorCS"),sQuery(id+"F0.wireOp",EDGE,"E52.MirrorCS"),sQuery(id+"F0.wireOp",EDGE,"E53.MirrorCS"),sQuery(id+"F0.wireOp",EDGE,"E54.MirrorCS"),sQuery(id+"F0.wireOp",EDGE,"E55.MirrorCS"),sQuery(id+"F0.wireOp",EDGE,"E56.MirrorCS"),sQuery(id+"F0.wireOp",EDGE,"E57.MirrorCS"),sQuery(id+"F0.wireOp",EDGE,"E58.MirrorCS"),sQuery(id+"F0.wireOp",EDGE,"E59.MirrorCS"),sQuery(id+"F0.wireOp",EDGE,"E60.MirrorCS"),sQuery(id+"F1.wireOp",VERTEX,"E122.start")])],"isStart":true});
            mirror(context, id + "F6", {"entities" : qUnion([Q0]), "mirrorPlane" : qUnion([Q1])});
        }
        {
            var Q0;
            Q0=makeQuery(id+"F0.imprint","IMPRINT",FACE,{"disambiguationData":[TD([[makeQuery(id+"F0.imprint","IMPRINT",EDGE,{"derivedFrom":sQuery(id+"F0.wireOp",EDGE,"E61.MirrorCS")}),1.0]])]});
            extrude(context, id + "F7", {"entities" : qUnion([Q0]), "oppositeDirection" : true, "depth" : 5 * mm, "offsetDistance" : 25 * mm});
        }
        {
            var Q0;
            Q0=makeQuery(id+"F7.opExtrude","CAP_FACE",FACE,{"disambiguationData":[OSD([sQuery(id+"F0.wireOp",EDGE,"E61.MirrorCS"),sQuery(id+"F0.wireOp",EDGE,"E62.MirrorCS"),sQuery(id+"F0.wireOp",EDGE,"E63.MirrorCS"),sQuery(id+"F0.wireOp",EDGE,"E64.MirrorCS"),sQuery(id+"F0.wireOp",EDGE,"E65.MirrorCS"),sQuery(id+"F0.wireOp",EDGE,"E66.MirrorCS"),sQuery(id+"F0.wireOp",EDGE,"E67.MirrorCS"),sQuery(id+"F0.wireOp",EDGE,"E68.MirrorCS"),sQuery(id+"F0.wireOp",EDGE,"E69.MirrorCS"),sQuery(id+"F0.wireOp",EDGE,"E70.MirrorCS"),sQuery(id+"F0.wireOp",EDGE,"E71.MirrorCS"),sQuery(id+"F0.wireOp",EDGE,"E72.MirrorCS"),sQuery(id+"F0.wireOp",EDGE,"E73.MirrorCS"),sQuery(id+"F0.wireOp",EDGE,"E74.MirrorCS"),sQuery(id+"F0.wireOp",EDGE,"E75.MirrorCS"),sQuery(id+"F0.wireOp",EDGE,"E76.MirrorCS"),sQuery(id+"F0.wireOp",EDGE,"E77.MirrorCS"),sQuery(id+"F0.wireOp",EDGE,"E78.MirrorCS"),sQuery(id+"F0.wireOp",EDGE,"E79.MirrorCS"),sQuery(id+"F0.wireOp",EDGE,"E80.MirrorCS"),sQuery(id+"F0.wireOp",EDGE,"E81.MirrorCS"),sQuery(id+"F0.wireOp",EDGE,"E82.MirrorCS"),sQuery(id+"F0.wireOp",EDGE,"E83.MirrorCS"),sQuery(id+"F0.wireOp",EDGE,"E84.MirrorCS"),sQuery(id+"F0.wireOp",EDGE,"E85.MirrorCS"),sQuery(id+"F0.wireOp",EDGE,"E86.MirrorCS"),sQuery(id+"F0.wireOp",EDGE,"E87.MirrorCS"),sQuery(id+"F0.wireOp",EDGE,"E88.MirrorCS"),sQuery(id+"F0.wireOp",EDGE,"E89.MirrorCS"),sQuery(id+"F0.wireOp",EDGE,"E90.MirrorCS"),sQuery(id+"F0.wireOp",EDGE,"E91.MirrorCS"),sQuery(id+"F0.wireOp",EDGE,"E92.MirrorCS"),sQuery(id+"F0.wireOp",EDGE,"E93.MirrorCS"),sQuery(id+"F0.wireOp",EDGE,"E94.MirrorCS"),sQuery(id+"F0.wireOp",EDGE,"E95.MirrorCS"),sQuery(id+"F0.wireOp",EDGE,"E96.MirrorCS"),sQuery(id+"F0.wireOp",EDGE,"E97.MirrorCS"),sQuery(id+"F0.wireOp",EDGE,"E98.MirrorCS"),sQuery(id+"F0.wireOp",EDGE,"E99.MirrorCS"),sQuery(id+"F0.wireOp",EDGE,"E100.MirrorCS"),sQuery(id+"F0.wireOp",EDGE,"E101.MirrorCS"),sQuery(id+"F0.wireOp",EDGE,"E102.MirrorCS"),sQuery(id+"F0.wireOp",EDGE,"E103.MirrorCS"),sQuery(id+"F0.wireOp",EDGE,"E104.MirrorCS"),sQuery(id+"F0.wireOp",EDGE,"E105.MirrorCS"),sQuery(id+"F0.wireOp",EDGE,"E106.MirrorCS"),sQuery(id+"F0.wireOp",EDGE,"E107.MirrorCS"),sQuery(id+"F0.wireOp",EDGE,"E108.MirrorCS"),sQuery(id+"F0.wireOp",EDGE,"E109.MirrorCS"),sQuery(id+"F0.wireOp",EDGE,"E110.MirrorCS"),sQuery(id+"F0.wireOp",EDGE,"E111.MirrorCS"),sQuery(id+"F0.wireOp",EDGE,"E112.MirrorCS"),sQuery(id+"F0.wireOp",EDGE,"E113.MirrorCS"),sQuery(id+"F0.wireOp",EDGE,"E114.MirrorCS"),sQuery(id+"F0.wireOp",EDGE,"E115.MirrorCS"),sQuery(id+"F0.wireOp",EDGE,"E116.MirrorCS"),sQuery(id+"F0.wireOp",EDGE,"E117.MirrorCS"),sQuery(id+"F0.wireOp",EDGE,"E118.MirrorCS"),sQuery(id+"F0.wireOp",EDGE,"E119.MirrorCS"),sQuery(id+"F0.wireOp",EDGE,"E120.MirrorCS"),sQuery(id+"F0.wireOp",EDGE,"E121.MirrorCS")])],"isStart":false});
            var sketch = newSketch(context, id + "F8", { "sketchPlane" : qUnion([Q0])});
            skLineSegment(sketch, "E185", {"start": v(212.64, -2.02) * mm, "end": v(213.27, -2.07) * mm});
            skLineSegment(sketch, "E186", {"start": v(213.27, -2.07) * mm, "end": v(215.09, -2.18) * mm});
            skLineSegment(sketch, "E187", {"start": v(215.09, -2.18) * mm, "end": v(218.04, -2.32) * mm});
            skLineSegment(sketch, "E188", {"start": v(218.04, -2.32) * mm, "end": v(222.12, -2.48) * mm});
            skLineSegment(sketch, "E189", {"start": v(222.12, -2.48) * mm, "end": v(227.27, -2.67) * mm});
            skLineSegment(sketch, "E190", {"start": v(227.27, -2.67) * mm, "end": v(233.43, -2.9) * mm});
            skLineSegment(sketch, "E191", {"start": v(233.43, -2.9) * mm, "end": v(240.52, -3.16) * mm});
            skLineSegment(sketch, "E192", {"start": v(240.52, -3.16) * mm, "end": v(248.46, -3.47) * mm});
            skLineSegment(sketch, "E193", {"start": v(248.46, -3.47) * mm, "end": v(257.15, -3.83) * mm});
            skLineSegment(sketch, "E194", {"start": v(257.15, -3.83) * mm, "end": v(266.47, -4.22) * mm});
            skLineSegment(sketch, "E195", {"start": v(266.47, -4.22) * mm, "end": v(276.3, -4.65) * mm});
            skLineSegment(sketch, "E196", {"start": v(276.3, -4.65) * mm, "end": v(286.55, -5.1) * mm});
            skLineSegment(sketch, "E197", {"start": v(286.55, -5.1) * mm, "end": v(297.07, -5.57) * mm});
            skLineSegment(sketch, "E198", {"start": v(297.07, -5.57) * mm, "end": v(307.74, -6.06) * mm});
            skLineSegment(sketch, "E199", {"start": v(307.74, -6.06) * mm, "end": v(318.42, -6.53) * mm});
            skLineSegment(sketch, "E200", {"start": v(318.42, -6.53) * mm, "end": v(328.98, -6.98) * mm});
            skLineSegment(sketch, "E201", {"start": v(328.98, -6.98) * mm, "end": v(339.31, -7.38) * mm});
            skLineSegment(sketch, "E202", {"start": v(339.31, -7.38) * mm, "end": v(349.29, -7.7) * mm});
            skLineSegment(sketch, "E203", {"start": v(349.29, -7.7) * mm, "end": v(358.8, -7.92) * mm});
            skLineSegment(sketch, "E204", {"start": v(358.8, -7.92) * mm, "end": v(367.75, -8.01) * mm});
            skLineSegment(sketch, "E205", {"start": v(367.75, -8.01) * mm, "end": v(376.06, -7.97) * mm});
            skLineSegment(sketch, "E206", {"start": v(376.06, -7.97) * mm, "end": v(383.63, -7.77) * mm});
            skLineSegment(sketch, "E207", {"start": v(383.63, -7.77) * mm, "end": v(390.43, -7.4) * mm});
            skLineSegment(sketch, "E208", {"start": v(390.43, -7.4) * mm, "end": v(396.4, -6.85) * mm});
            skLineSegment(sketch, "E209", {"start": v(396.4, -6.85) * mm, "end": v(401.5, -6.15) * mm});
            skLineSegment(sketch, "E210", {"start": v(401.5, -6.15) * mm, "end": v(405.72, -5.33) * mm});
            skLineSegment(sketch, "E211", {"start": v(405.72, -5.33) * mm, "end": v(408.98, -4.42) * mm});
            skLineSegment(sketch, "E212", {"start": v(408.98, -4.42) * mm, "end": v(411.26, -3.47) * mm});
            skLineSegment(sketch, "E213", {"start": v(411.26, -3.47) * mm, "end": v(412.49, -2.54) * mm});
            skLineSegment(sketch, "E214", {"start": v(412.49, -2.54) * mm, "end": v(412.64, -2.02) * mm});
            skLineSegment(sketch, "E215", {"start": v(412.64, -2.02) * mm, "end": v(412.52, -1.5) * mm});
            skLineSegment(sketch, "E216", {"start": v(412.52, -1.5) * mm, "end": v(411.46, -0.22) * mm});
            skLineSegment(sketch, "E217", {"start": v(411.46, -0.22) * mm, "end": v(409.53, 1.2) * mm});
            skLineSegment(sketch, "E218", {"start": v(409.53, 1.2) * mm, "end": v(397.23, 10.27) * mm});
            skFitSpline(sketch, "E219", {"points": [v(397.23, 10.27) * mm, v(304.45, 39.07) * mm, v(189.15, 41.7) * mm, v(212.64, -2.02) * mm], "startDerivative": vector(-168.43, 114.69) * mm, "endDerivative": vector(-17.43, -380.77) * mm});
            skSolve(sketch);
        }
        {
            var Q0;
            Q0 = qSketchRegion(id + "F8", true);
            extrude(context, id + "F9", {"entities" : qUnion([Q0]), "operationType" : NewBodyOperationType.ADD, "depth" : 2 * mm, "offsetDistance" : 25 * mm});
        }
        {
            var Q0;
            Q0=makeQuery(id+"F9.opExtrude","CAP_EDGE",EDGE,{"disambiguationData":[OSD([sQuery(id+"F8.wireOp",EDGE,"E219")])],"isStart":true});
            var Q1;
            Q1=makeQuery(id+"F9.opExtrude","CAP_EDGE",EDGE,{"disambiguationData":[OSD([sQuery(id+"F8.wireOp",EDGE,"E217"),sQuery(id+"F8.wireOp",EDGE,"E218")])],"isStart":true});
            var Q2;
            Q2=makeQuery(id+"F9.opExtrude","CAP_EDGE",EDGE,{"disambiguationData":[OSD([sQuery(id+"F8.wireOp",EDGE,"E217"),sQuery(id+"F8.wireOp",EDGE,"E218")])],"isStart":false});
            var Q3;
            Q3=makeQuery(id+"F9.opExtrude","CAP_EDGE",EDGE,{"disambiguationData":[OSD([sQuery(id+"F8.wireOp",EDGE,"E219")])],"isStart":false});
            chamfer(context, id + "F10", {"entities" : qUnion([Q0, Q1, Q2, Q3]), "width" : 0.8 * mm, "tangentPropagation" : true});
        }
        {
            var Q0;
            Q0=makeQuery(id+"F0.imprint","IMPRINT",FACE,{"disambiguationData":[TD([[makeQuery(id+"F0.imprint","IMPRINT",EDGE,{"derivedFrom":sQuery(id+"F0.wireOp",EDGE,"E61.MirrorCS")}),1.0]])]});
            var sketch = newSketch(context, id + "F11", { "sketchPlane" : qUnion([Q0])});
            skCircle(sketch, "E220", {"center": v(-366.4, 0) * mm, "radius": 2 * mm});
            skSolve(sketch);
        }
        {
            var Q0;
            Q0 = qSketchRegion(id + "F11", true);
            extrude(context, id + "F12", {"entities" : qUnion([Q0]), "operationType" : NewBodyOperationType.REMOVE, "oppositeDirection" : true, "depth" : 25 * mm, "offsetDistance" : 25 * mm});
        }
        {
            var Q0;
            Q0=makeQuery(id+"F7.opExtrude","SWEPT_BODY",BODY,{"disambiguationData":[OSD([sQuery(id+"F0.wireOp",EDGE,"E61.MirrorCS"),sQuery(id+"F0.wireOp",EDGE,"E62.MirrorCS"),sQuery(id+"F0.wireOp",EDGE,"E63.MirrorCS"),sQuery(id+"F0.wireOp",EDGE,"E64.MirrorCS"),sQuery(id+"F0.wireOp",EDGE,"E65.MirrorCS"),sQuery(id+"F0.wireOp",EDGE,"E66.MirrorCS"),sQuery(id+"F0.wireOp",EDGE,"E67.MirrorCS"),sQuery(id+"F0.wireOp",EDGE,"E68.MirrorCS"),sQuery(id+"F0.wireOp",EDGE,"E69.MirrorCS"),sQuery(id+"F0.wireOp",EDGE,"E70.MirrorCS"),sQuery(id+"F0.wireOp",EDGE,"E71.MirrorCS"),sQuery(id+"F0.wireOp",EDGE,"E72.MirrorCS"),sQuery(id+"F0.wireOp",EDGE,"E73.MirrorCS"),sQuery(id+"F0.wireOp",EDGE,"E74.MirrorCS"),sQuery(id+"F0.wireOp",EDGE,"E75.MirrorCS"),sQuery(id+"F0.wireOp",EDGE,"E76.MirrorCS"),sQuery(id+"F0.wireOp",EDGE,"E77.MirrorCS"),sQuery(id+"F0.wireOp",EDGE,"E78.MirrorCS"),sQuery(id+"F0.wireOp",EDGE,"E79.MirrorCS"),sQuery(id+"F0.wireOp",EDGE,"E80.MirrorCS"),sQuery(id+"F0.wireOp",EDGE,"E81.MirrorCS"),sQuery(id+"F0.wireOp",EDGE,"E82.MirrorCS"),sQuery(id+"F0.wireOp",EDGE,"E83.MirrorCS"),sQuery(id+"F0.wireOp",EDGE,"E84.MirrorCS"),sQuery(id+"F0.wireOp",EDGE,"E85.MirrorCS"),sQuery(id+"F0.wireOp",EDGE,"E86.MirrorCS"),sQuery(id+"F0.wireOp",EDGE,"E87.MirrorCS"),sQuery(id+"F0.wireOp",EDGE,"E88.MirrorCS"),sQuery(id+"F0.wireOp",EDGE,"E89.MirrorCS"),sQuery(id+"F0.wireOp",EDGE,"E90.MirrorCS"),sQuery(id+"F0.wireOp",EDGE,"E91.MirrorCS"),sQuery(id+"F0.wireOp",EDGE,"E92.MirrorCS"),sQuery(id+"F0.wireOp",EDGE,"E93.MirrorCS"),sQuery(id+"F0.wireOp",EDGE,"E94.MirrorCS"),sQuery(id+"F0.wireOp",EDGE,"E95.MirrorCS"),sQuery(id+"F0.wireOp",EDGE,"E96.MirrorCS"),sQuery(id+"F0.wireOp",EDGE,"E97.MirrorCS"),sQuery(id+"F0.wireOp",EDGE,"E98.MirrorCS"),sQuery(id+"F0.wireOp",EDGE,"E99.MirrorCS"),sQuery(id+"F0.wireOp",EDGE,"E100.MirrorCS"),sQuery(id+"F0.wireOp",EDGE,"E101.MirrorCS"),sQuery(id+"F0.wireOp",EDGE,"E102.MirrorCS"),sQuery(id+"F0.wireOp",EDGE,"E103.MirrorCS"),sQuery(id+"F0.wireOp",EDGE,"E104.MirrorCS"),sQuery(id+"F0.wireOp",EDGE,"E105.MirrorCS"),sQuery(id+"F0.wireOp",EDGE,"E106.MirrorCS"),sQuery(id+"F0.wireOp",EDGE,"E107.MirrorCS"),sQuery(id+"F0.wireOp",EDGE,"E108.MirrorCS"),sQuery(id+"F0.wireOp",EDGE,"E109.MirrorCS"),sQuery(id+"F0.wireOp",EDGE,"E110.MirrorCS"),sQuery(id+"F0.wireOp",EDGE,"E111.MirrorCS"),sQuery(id+"F0.wireOp",EDGE,"E112.MirrorCS"),sQuery(id+"F0.wireOp",EDGE,"E113.MirrorCS"),sQuery(id+"F0.wireOp",EDGE,"E114.MirrorCS"),sQuery(id+"F0.wireOp",EDGE,"E115.MirrorCS"),sQuery(id+"F0.wireOp",EDGE,"E116.MirrorCS"),sQuery(id+"F0.wireOp",EDGE,"E117.MirrorCS"),sQuery(id+"F0.wireOp",EDGE,"E118.MirrorCS"),sQuery(id+"F0.wireOp",EDGE,"E119.MirrorCS"),sQuery(id+"F0.wireOp",EDGE,"E120.MirrorCS"),sQuery(id+"F0.wireOp",EDGE,"E121.MirrorCS")])]});
            var Q1;
            Q1=makeQuery(id+"F0.imprint","IMPRINT",FACE,{"disambiguationData":[TD([[makeQuery(id+"F0.imprint","IMPRINT",EDGE,{"derivedFrom":sQuery(id+"F0.wireOp",EDGE,"E61.MirrorCS")}),1.0]])]});
            mirror(context, id + "F13", {"entities" : qUnion([Q0]), "mirrorPlane" : qUnion([Q1])});
        }
    });
